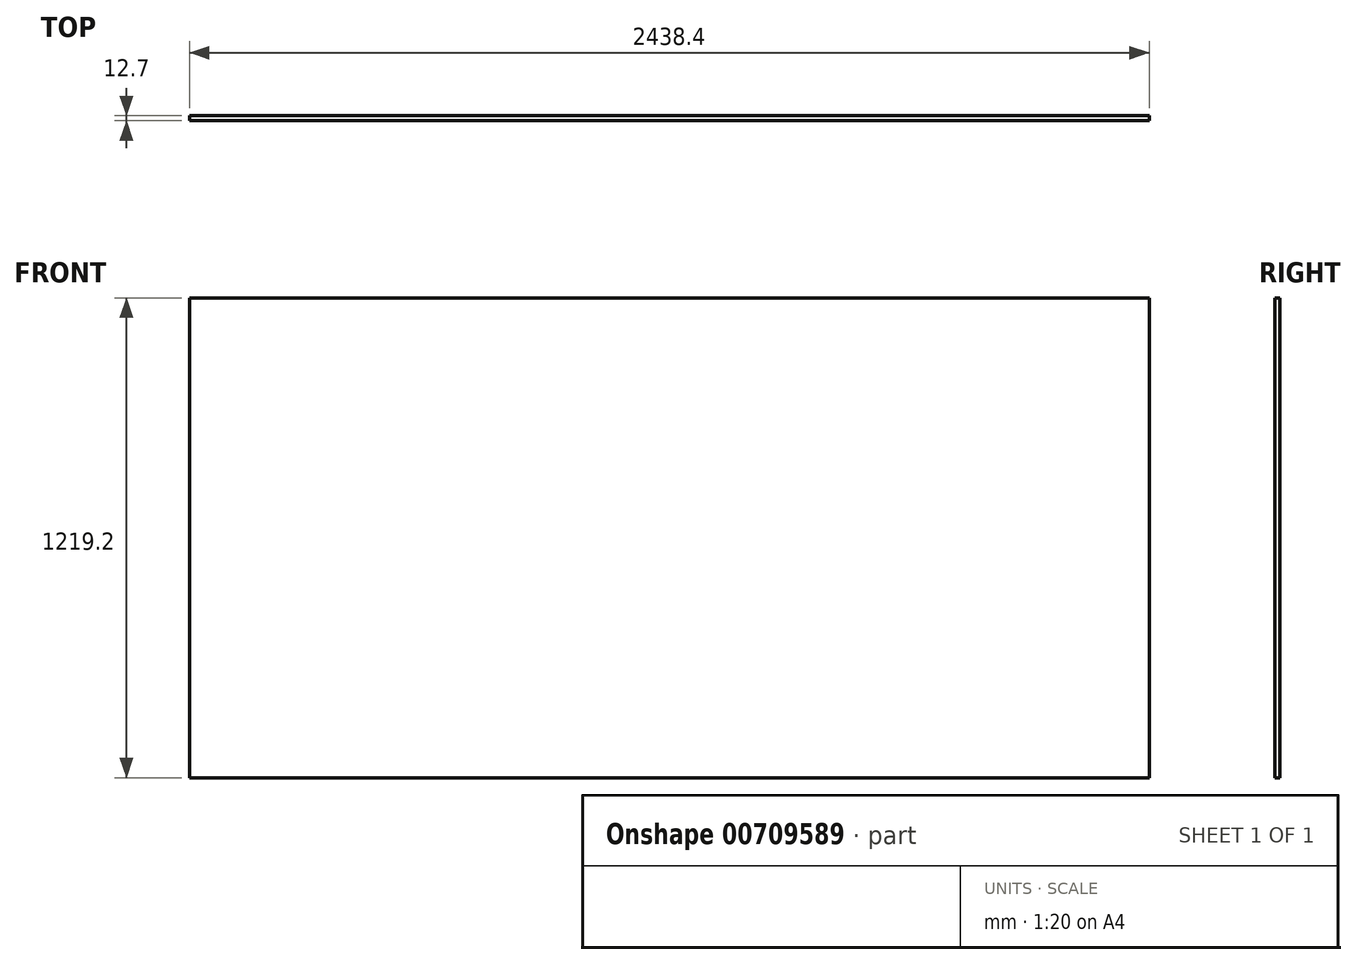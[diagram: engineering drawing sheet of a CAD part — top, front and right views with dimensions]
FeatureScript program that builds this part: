
annotation { "Feature Type Name" : "Feature", "Feature Type Description" : "" }
export const myFeature = defineFeature(function(context is Context, id is Id, definition is map)
    precondition{}
    {
        {
            var Q0;
            Q0=qCreatedBy(makeId("Front.planeOp"),FACE);
            var sketch = newSketch(context, id + "F0", { "sketchPlane" : qUnion([Q0])});
            skLineSegment(sketch, "E0.bottom", {"start": v(0, 0) * mm, "end": v(2438.4, 0) * mm});
            skLineSegment(sketch, "E0.top", {"start": v(0, 1219.2) * mm, "end": v(2438.4, 1219.2) * mm});
            skLineSegment(sketch, "E0.left", {"start": v(0, 0) * mm, "end": v(0, 1219.2) * mm});
            skLineSegment(sketch, "E0.right", {"start": v(2438.4, 0) * mm, "end": v(2438.4, 1219.2) * mm});
            skSolve(sketch);
        }
        {
            var Q0;
            Q0 = qSketchRegion(id + "F0", true);
            extrude(context, id + "F1", {"entities" : qUnion([Q0]), "depth" : 12.7 * mm, "offsetDistance" : 25.4 * mm});
        }
    });
